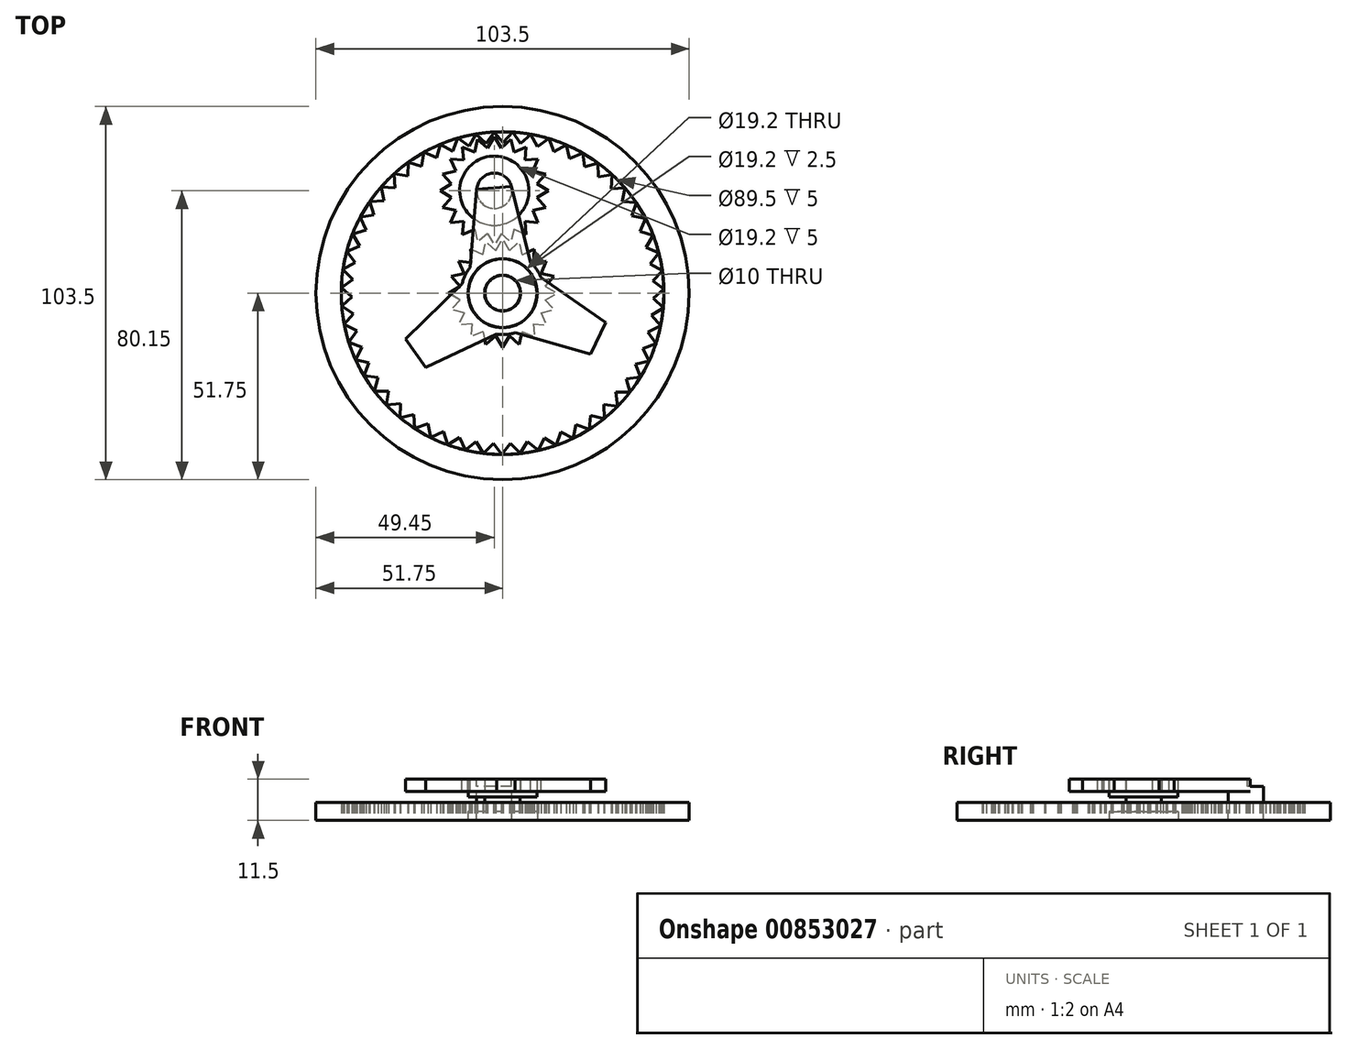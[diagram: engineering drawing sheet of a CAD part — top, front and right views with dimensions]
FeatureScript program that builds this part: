
annotation { "Feature Type Name" : "Feature", "Feature Type Description" : "" }
export const myFeature = defineFeature(function(context is Context, id is Id, definition is map)
    precondition{}
    {
        {
            var Q0;
            Q0=qCreatedBy(makeId("Top.planeOp"),FACE);
            var sketch = newSketch(context, id + "F0", { "sketchPlane" : qUnion([Q0])});
            skCircle(sketch, "E0", {"center": v(0, 0) * mm, "radius": 15 * mm});
            skLineSegment(sketch, "E1", {"start": v(0, 0) * mm, "end": v(0, 15) * mm, "construction": true});
            skCircle(sketch, "E2", {"center": v(0, 0) * mm, "radius": 12 * mm});
            skLineSegment(sketch, "E3", {"start": v(0, 0) * mm, "end": v(1.88, 11.85) * mm, "construction": true});
            skLineSegment(sketch, "E4", {"start": v(1.88, 11.85) * mm, "end": v(0, 15) * mm});
            skLineSegment(sketch, "E5.MirrorCS", {"start": v(-1.88, 11.85) * mm, "end": v(0, 15) * mm});
            skLineSegment(sketch, "E6.1.0", {"start": v(5.45, 10.7) * mm, "end": v(4.64, 14.27) * mm});
            skLineSegment(sketch, "E6.1.1", {"start": v(1.88, 11.85) * mm, "end": v(4.64, 14.27) * mm});
            skLineSegment(sketch, "E6.2.0", {"start": v(8.49, 8.49) * mm, "end": v(8.82, 12.14) * mm});
            skLineSegment(sketch, "E6.2.1", {"start": v(5.45, 10.7) * mm, "end": v(8.82, 12.14) * mm});
            skLineSegment(sketch, "E6.3.0", {"start": v(10.7, 5.45) * mm, "end": v(12.14, 8.82) * mm});
            skLineSegment(sketch, "E6.3.1", {"start": v(8.49, 8.49) * mm, "end": v(12.14, 8.82) * mm});
            skLineSegment(sketch, "E6.4.0", {"start": v(11.85, 1.88) * mm, "end": v(14.27, 4.64) * mm});
            skLineSegment(sketch, "E6.4.1", {"start": v(10.7, 5.45) * mm, "end": v(14.27, 4.64) * mm});
            skLineSegment(sketch, "E6.5.0", {"start": v(11.85, -1.88) * mm, "end": v(15, 0) * mm});
            skLineSegment(sketch, "E6.5.1", {"start": v(11.85, 1.88) * mm, "end": v(15, 0) * mm});
            skLineSegment(sketch, "E6.6.0", {"start": v(10.7, -5.45) * mm, "end": v(14.27, -4.64) * mm});
            skLineSegment(sketch, "E6.6.1", {"start": v(11.85, -1.88) * mm, "end": v(14.27, -4.64) * mm});
            skLineSegment(sketch, "E6.7.0", {"start": v(8.49, -8.49) * mm, "end": v(12.14, -8.82) * mm});
            skLineSegment(sketch, "E6.7.1", {"start": v(10.7, -5.45) * mm, "end": v(12.14, -8.82) * mm});
            skLineSegment(sketch, "E6.8.0", {"start": v(5.45, -10.7) * mm, "end": v(8.82, -12.14) * mm});
            skLineSegment(sketch, "E6.8.1", {"start": v(8.49, -8.49) * mm, "end": v(8.82, -12.14) * mm});
            skLineSegment(sketch, "E6.9.0", {"start": v(1.88, -11.85) * mm, "end": v(4.64, -14.27) * mm});
            skLineSegment(sketch, "E6.9.1", {"start": v(5.45, -10.7) * mm, "end": v(4.64, -14.27) * mm});
            skLineSegment(sketch, "E6.anchor2", {"start": v(0, 0) * mm, "end": v(1.88, -11.85) * mm, "construction": true});
            skLineSegment(sketch, "E7.MirrorCS", {"start": v(-1.88, 11.85) * mm, "end": v(-4.64, 14.27) * mm});
            skLineSegment(sketch, "E8.MirrorCS", {"start": v(-5.45, 10.7) * mm, "end": v(-4.64, 14.27) * mm});
            skLineSegment(sketch, "E9.MirrorCS", {"start": v(-5.45, 10.7) * mm, "end": v(-8.82, 12.14) * mm});
            skLineSegment(sketch, "E10.MirrorCS", {"start": v(-8.49, 8.49) * mm, "end": v(-8.82, 12.14) * mm});
            skLineSegment(sketch, "E11.MirrorCS", {"start": v(-8.49, 8.49) * mm, "end": v(-12.14, 8.82) * mm});
            skLineSegment(sketch, "E12.MirrorCS", {"start": v(-10.7, 5.45) * mm, "end": v(-12.14, 8.82) * mm});
            skLineSegment(sketch, "E13.MirrorCS", {"start": v(-10.7, 5.45) * mm, "end": v(-14.27, 4.64) * mm});
            skLineSegment(sketch, "E14.MirrorCS", {"start": v(-11.85, 1.88) * mm, "end": v(-14.27, 4.64) * mm});
            skLineSegment(sketch, "E15.MirrorCS", {"start": v(-11.85, 1.88) * mm, "end": v(-15, 0) * mm});
            skLineSegment(sketch, "E16.MirrorCS", {"start": v(-11.85, -1.88) * mm, "end": v(-15, 0) * mm});
            skLineSegment(sketch, "E17.MirrorCS", {"start": v(-11.85, -1.88) * mm, "end": v(-14.27, -4.64) * mm});
            skLineSegment(sketch, "E18.MirrorCS", {"start": v(-10.7, -5.45) * mm, "end": v(-14.27, -4.64) * mm});
            skLineSegment(sketch, "E19.MirrorCS", {"start": v(-10.7, -5.45) * mm, "end": v(-12.14, -8.82) * mm});
            skLineSegment(sketch, "E20.MirrorCS", {"start": v(-8.49, -8.49) * mm, "end": v(-12.14, -8.82) * mm});
            skLineSegment(sketch, "E21.MirrorCS", {"start": v(-8.49, -8.49) * mm, "end": v(-8.82, -12.14) * mm});
            skLineSegment(sketch, "E22.MirrorCS", {"start": v(-5.45, -10.7) * mm, "end": v(-8.82, -12.14) * mm});
            skLineSegment(sketch, "E23.MirrorCS", {"start": v(-5.45, -10.7) * mm, "end": v(-4.64, -14.27) * mm});
            skLineSegment(sketch, "E24.MirrorCS", {"start": v(-1.88, -11.85) * mm, "end": v(-4.64, -14.27) * mm});
            skLineSegment(sketch, "E25.MirrorCS", {"start": v(-1.88, -11.85) * mm, "end": v(0, -15) * mm});
            skLineSegment(sketch, "E26.MirrorCS", {"start": v(1.88, -11.85) * mm, "end": v(0, -15) * mm});
            skCircle(sketch, "E27", {"center": v(0, 0) * mm, "radius": 9.6 * mm});
            skSolve(sketch);
        }
        {
            var Q0;
            {var subQ0=sQuery(id+"F0.wireOp",EDGE,"E2");var subQ8=makeQuery(id+"F0.imprint","INTERSECT",VERTEX,{"derivedFrom":[subQ0,sQuery(id+"F0.wireOp",EDGE,"E6.3.0"),sQuery(id+"F0.wireOp",EDGE,"E6.4.1")]});Q0=makeQuery(id+"F0.imprint","IMPRINT",FACE,{"disambiguationData":[TD([[makeQuery(id+"F0.imprint","IMPRINT",EDGE,{"disambiguationData":[TD([[subQ8,1.0]])],"derivedFrom":subQ0}),1.0]])]});}
            var Q1;
            {var subQ0=sQuery(id+"F0.wireOp",EDGE,"E7.MirrorCS");Q1=makeQuery(id+"F0.imprint","IMPRINT",FACE,{"disambiguationData":[TD([[makeQuery(id+"F0.imprint","IMPRINT",EDGE,{"derivedFrom":subQ0}),1.0]])]});}
            var Q2;
            {var subQ0=sQuery(id+"F0.wireOp",EDGE,"E4");Q2=makeQuery(id+"F0.imprint","IMPRINT",FACE,{"disambiguationData":[TD([[makeQuery(id+"F0.imprint","IMPRINT",EDGE,{"derivedFrom":subQ0}),1.0]])]});}
            var Q3;
            {var subQ2=sQuery(id+"F0.wireOp",EDGE,"E6.1.0");Q3=makeQuery(id+"F0.imprint","IMPRINT",FACE,{"disambiguationData":[TD([[makeQuery(id+"F0.imprint","IMPRINT",EDGE,{"derivedFrom":subQ2}),1.0]])]});}
            var Q4;
            {var subQ2=sQuery(id+"F0.wireOp",EDGE,"E6.2.0");Q4=makeQuery(id+"F0.imprint","IMPRINT",FACE,{"disambiguationData":[TD([[makeQuery(id+"F0.imprint","IMPRINT",EDGE,{"derivedFrom":subQ2}),1.0]])]});}
            var Q5;
            {var subQ2=sQuery(id+"F0.wireOp",EDGE,"E6.3.0");Q5=makeQuery(id+"F0.imprint","IMPRINT",FACE,{"disambiguationData":[TD([[makeQuery(id+"F0.imprint","IMPRINT",EDGE,{"derivedFrom":subQ2}),1.0]])]});}
            var Q6;
            {var subQ2=sQuery(id+"F0.wireOp",EDGE,"E6.4.0");Q6=makeQuery(id+"F0.imprint","IMPRINT",FACE,{"disambiguationData":[TD([[makeQuery(id+"F0.imprint","IMPRINT",EDGE,{"derivedFrom":subQ2}),1.0]])]});}
            var Q7;
            {var subQ2=sQuery(id+"F0.wireOp",EDGE,"E6.5.0");Q7=makeQuery(id+"F0.imprint","IMPRINT",FACE,{"disambiguationData":[TD([[makeQuery(id+"F0.imprint","IMPRINT",EDGE,{"derivedFrom":subQ2}),1.0]])]});}
            var Q8;
            {var subQ2=sQuery(id+"F0.wireOp",EDGE,"E6.6.0");Q8=makeQuery(id+"F0.imprint","IMPRINT",FACE,{"disambiguationData":[TD([[makeQuery(id+"F0.imprint","IMPRINT",EDGE,{"derivedFrom":subQ2}),1.0]])]});}
            var Q9;
            {var subQ2=sQuery(id+"F0.wireOp",EDGE,"E6.7.0");Q9=makeQuery(id+"F0.imprint","IMPRINT",FACE,{"disambiguationData":[TD([[makeQuery(id+"F0.imprint","IMPRINT",EDGE,{"derivedFrom":subQ2}),1.0]])]});}
            var Q10;
            {var subQ2=sQuery(id+"F0.wireOp",EDGE,"E6.8.0");Q10=makeQuery(id+"F0.imprint","IMPRINT",FACE,{"disambiguationData":[TD([[makeQuery(id+"F0.imprint","IMPRINT",EDGE,{"derivedFrom":subQ2}),1.0]])]});}
            var Q11;
            {var subQ2=sQuery(id+"F0.wireOp",EDGE,"E6.9.0");Q11=makeQuery(id+"F0.imprint","IMPRINT",FACE,{"disambiguationData":[TD([[makeQuery(id+"F0.imprint","IMPRINT",EDGE,{"derivedFrom":subQ2}),1.0]])]});}
            var Q12;
            {var subQ2=sQuery(id+"F0.wireOp",EDGE,"E25.MirrorCS");Q12=makeQuery(id+"F0.imprint","IMPRINT",FACE,{"disambiguationData":[TD([[makeQuery(id+"F0.imprint","IMPRINT",EDGE,{"derivedFrom":subQ2}),1.0]])]});}
            var Q13;
            {var subQ0=sQuery(id+"F0.wireOp",EDGE,"E23.MirrorCS");Q13=makeQuery(id+"F0.imprint","IMPRINT",FACE,{"disambiguationData":[TD([[makeQuery(id+"F0.imprint","IMPRINT",EDGE,{"derivedFrom":subQ0}),1.0]])]});}
            var Q14;
            {var subQ0=sQuery(id+"F0.wireOp",EDGE,"E21.MirrorCS");Q14=makeQuery(id+"F0.imprint","IMPRINT",FACE,{"disambiguationData":[TD([[makeQuery(id+"F0.imprint","IMPRINT",EDGE,{"derivedFrom":subQ0}),1.0]])]});}
            var Q15;
            {var subQ0=sQuery(id+"F0.wireOp",EDGE,"E19.MirrorCS");Q15=makeQuery(id+"F0.imprint","IMPRINT",FACE,{"disambiguationData":[TD([[makeQuery(id+"F0.imprint","IMPRINT",EDGE,{"derivedFrom":subQ0}),1.0]])]});}
            var Q16;
            {var subQ0=sQuery(id+"F0.wireOp",EDGE,"E17.MirrorCS");Q16=makeQuery(id+"F0.imprint","IMPRINT",FACE,{"disambiguationData":[TD([[makeQuery(id+"F0.imprint","IMPRINT",EDGE,{"derivedFrom":subQ0}),1.0]])]});}
            var Q17;
            {var subQ0=sQuery(id+"F0.wireOp",EDGE,"E15.MirrorCS");Q17=makeQuery(id+"F0.imprint","IMPRINT",FACE,{"disambiguationData":[TD([[makeQuery(id+"F0.imprint","IMPRINT",EDGE,{"derivedFrom":subQ0}),1.0]])]});}
            var Q18;
            {var subQ0=sQuery(id+"F0.wireOp",EDGE,"E13.MirrorCS");Q18=makeQuery(id+"F0.imprint","IMPRINT",FACE,{"disambiguationData":[TD([[makeQuery(id+"F0.imprint","IMPRINT",EDGE,{"derivedFrom":subQ0}),1.0]])]});}
            var Q19;
            {var subQ0=sQuery(id+"F0.wireOp",EDGE,"E11.MirrorCS");Q19=makeQuery(id+"F0.imprint","IMPRINT",FACE,{"disambiguationData":[TD([[makeQuery(id+"F0.imprint","IMPRINT",EDGE,{"derivedFrom":subQ0}),1.0]])]});}
            var Q20;
            {var subQ0=sQuery(id+"F0.wireOp",EDGE,"E9.MirrorCS");Q20=makeQuery(id+"F0.imprint","IMPRINT",FACE,{"disambiguationData":[TD([[makeQuery(id+"F0.imprint","IMPRINT",EDGE,{"derivedFrom":subQ0}),1.0]])]});}
            extrude(context, id + "F1", {"entities" : qUnion([Q0, Q1, Q2, Q3, Q4, Q5, Q6, Q7, Q8, Q9, Q10, Q11, Q12, Q13, Q14, Q15, Q16, Q17, Q18, Q19, Q20]), "endBound" : BoundingType.SYMMETRIC, "depth" : 5 * mm, "offsetDistance" : 25 * mm});
        }
        {
            var Q0;
            Q0=qCreatedBy(makeId("Front.planeOp"),FACE);
            var sketch = newSketch(context, id + "F2", { "sketchPlane" : qUnion([Q0])});
            skLineSegment(sketch, "E28", {"start": v(0, 0) * mm, "end": v(0, 25.45) * mm, "construction": true});
            skSolve(sketch);
        }
        {
            var Q0;
            Q0=qCreatedBy(makeId("Top.planeOp"),FACE);
            var sketch = newSketch(context, id + "F3", { "sketchPlane" : qUnion([Q0])});
            skCircle(sketch, "E29", {"center": v(0, 0) * mm, "radius": 41.75 * mm});
            skCircle(sketch, "E30.0", {"center": v(0, 0) * mm, "radius": 51.75 * mm});
            skCircle(sketch, "E31.0", {"center": v(0, 0) * mm, "radius": 44.75 * mm});
            skLineSegment(sketch, "E32", {"start": v(0, 0) * mm, "end": v(44.55, -4.2) * mm, "construction": true});
            skLineSegment(sketch, "E33", {"start": v(0, 0) * mm, "end": v(44.24, -6.74) * mm, "construction": true});
            skLineSegment(sketch, "E34", {"start": v(0, 0) * mm, "end": v(44.75, 0) * mm, "construction": true});
            skLineSegment(sketch, "E35", {"start": v(44.24, -6.74) * mm, "end": v(41.57, -3.92) * mm});
            skLineSegment(sketch, "E36.MirrorCS", {"start": v(44.72, -1.64) * mm, "end": v(41.57, -3.92) * mm});
            skLineSegment(sketch, "E37.1.0", {"start": v(43.16, -11.83) * mm, "end": v(40.83, -8.72) * mm});
            skLineSegment(sketch, "E37.1.1", {"start": v(44.23, -6.82) * mm, "end": v(40.83, -8.72) * mm});
            skLineSegment(sketch, "E37.2.0", {"start": v(41.5, -16.76) * mm, "end": v(39.54, -13.4) * mm});
            skLineSegment(sketch, "E37.2.1", {"start": v(43.14, -11.9) * mm, "end": v(39.54, -13.4) * mm});
            skLineSegment(sketch, "E37.3.0", {"start": v(39.26, -21.47) * mm, "end": v(37.72, -17.9) * mm});
            skLineSegment(sketch, "E37.3.1", {"start": v(41.46, -16.83) * mm, "end": v(37.72, -17.9) * mm});
            skLineSegment(sketch, "E37.4.0", {"start": v(36.5, -25.88) * mm, "end": v(35.39, -22.15) * mm});
            skLineSegment(sketch, "E37.4.1", {"start": v(39.23, -21.53) * mm, "end": v(35.39, -22.15) * mm});
            skLineSegment(sketch, "E37.5.0", {"start": v(33.25, -29.94) * mm, "end": v(32.58, -26.11) * mm});
            skLineSegment(sketch, "E37.5.1", {"start": v(36.46, -25.94) * mm, "end": v(32.58, -26.11) * mm});
            skLineSegment(sketch, "E37.6.0", {"start": v(29.55, -33.6) * mm, "end": v(29.32, -29.72) * mm});
            skLineSegment(sketch, "E37.6.1", {"start": v(33.2, -30) * mm, "end": v(29.32, -29.72) * mm});
            skLineSegment(sketch, "E37.7.0", {"start": v(25.45, -36.8) * mm, "end": v(25.68, -32.92) * mm});
            skLineSegment(sketch, "E37.7.1", {"start": v(29.5, -33.65) * mm, "end": v(25.68, -32.92) * mm});
            skLineSegment(sketch, "E37.8.0", {"start": v(21, -39.51) * mm, "end": v(21.68, -35.68) * mm});
            skLineSegment(sketch, "E37.8.1", {"start": v(25.4, -36.85) * mm, "end": v(21.68, -35.68) * mm});
            skLineSegment(sketch, "E37.9.0", {"start": v(16.28, -41.68) * mm, "end": v(17.4, -37.96) * mm});
            skLineSegment(sketch, "E37.9.1", {"start": v(20.94, -39.55) * mm, "end": v(17.4, -37.96) * mm});
            skLineSegment(sketch, "E37.anchor2", {"start": v(0, 0) * mm, "end": v(16.28, -41.68) * mm, "construction": true});
            skLineSegment(sketch, "E38.1.0", {"start": v(16.33, -41.66) * mm, "end": v(12.98, -39.68) * mm});
            skLineSegment(sketch, "E38.1.1", {"start": v(11.46, -43.26) * mm, "end": v(12.98, -39.68) * mm});
            skLineSegment(sketch, "E38.1.2", {"start": v(11.38, -43.28) * mm, "end": v(8.29, -40.92) * mm});
            skLineSegment(sketch, "E38.1.3", {"start": v(6.36, -44.3) * mm, "end": v(8.29, -40.92) * mm});
            skLineSegment(sketch, "E38.1.4", {"start": v(6.28, -44.3) * mm, "end": v(3.48, -41.6) * mm});
            skLineSegment(sketch, "E38.1.5", {"start": v(1.17, -44.73) * mm, "end": v(3.48, -41.6) * mm});
            skLineSegment(sketch, "E38.1.6", {"start": v(1.1, -44.74) * mm, "end": v(-1.37, -41.73) * mm});
            skLineSegment(sketch, "E38.1.7", {"start": v(-4.03, -44.57) * mm, "end": v(-1.37, -41.73) * mm});
            skLineSegment(sketch, "E38.1.8", {"start": v(-4.1, -44.56) * mm, "end": v(-6.2, -41.29) * mm});
            skLineSegment(sketch, "E38.1.9", {"start": v(-9.18, -43.8) * mm, "end": v(-6.2, -41.29) * mm});
            skLineSegment(sketch, "E38.1.10", {"start": v(-9.25, -43.78) * mm, "end": v(-10.96, -40.29) * mm});
            skLineSegment(sketch, "E38.1.11", {"start": v(-14.2, -42.44) * mm, "end": v(-10.96, -40.29) * mm});
            skLineSegment(sketch, "E38.1.12", {"start": v(-14.27, -42.41) * mm, "end": v(-15.56, -38.74) * mm});
            skLineSegment(sketch, "E38.1.13", {"start": v(-19.03, -40.5) * mm, "end": v(-15.56, -38.74) * mm});
            skLineSegment(sketch, "E38.1.14", {"start": v(-19.1, -40.47) * mm, "end": v(-19.95, -36.67) * mm});
            skLineSegment(sketch, "E38.1.15", {"start": v(-23.6, -38.02) * mm, "end": v(-19.95, -36.67) * mm});
            skLineSegment(sketch, "E38.1.16", {"start": v(-23.67, -37.98) * mm, "end": v(-24.08, -34.1) * mm});
            skLineSegment(sketch, "E38.1.17", {"start": v(-27.86, -35.02) * mm, "end": v(-24.08, -34.1) * mm});
            skLineSegment(sketch, "E38.1.18", {"start": v(-27.92, -34.97) * mm, "end": v(-27.87, -31.08) * mm});
            skLineSegment(sketch, "E38.1.19", {"start": v(-31.74, -31.55) * mm, "end": v(-27.87, -31.08) * mm});
            skLineSegment(sketch, "E38.2.0", {"start": v(-31.7, -31.59) * mm, "end": v(-31.21, -27.73) * mm});
            skLineSegment(sketch, "E38.2.1", {"start": v(-35.1, -27.75) * mm, "end": v(-31.21, -27.73) * mm});
            skLineSegment(sketch, "E38.2.2", {"start": v(-35.15, -27.7) * mm, "end": v(-34.22, -23.92) * mm});
            skLineSegment(sketch, "E38.2.3", {"start": v(-38.09, -23.5) * mm, "end": v(-34.22, -23.92) * mm});
            skLineSegment(sketch, "E38.2.4", {"start": v(-38.13, -23.43) * mm, "end": v(-36.77, -19.78) * mm});
            skLineSegment(sketch, "E38.2.5", {"start": v(-40.56, -18.91) * mm, "end": v(-36.77, -19.78) * mm});
            skLineSegment(sketch, "E38.2.6", {"start": v(-40.59, -18.84) * mm, "end": v(-38.81, -15.38) * mm});
            skLineSegment(sketch, "E38.2.7", {"start": v(-42.48, -14.07) * mm, "end": v(-38.81, -15.38) * mm});
            skLineSegment(sketch, "E38.2.8", {"start": v(-42.5, -14) * mm, "end": v(-40.34, -10.77) * mm});
            skLineSegment(sketch, "E38.2.9", {"start": v(-43.83, -9.05) * mm, "end": v(-40.34, -10.77) * mm});
            skLineSegment(sketch, "E38.2.10", {"start": v(-43.84, -8.97) * mm, "end": v(-41.31, -6.01) * mm});
            skLineSegment(sketch, "E38.2.11", {"start": v(-44.58, -3.9) * mm, "end": v(-41.31, -6.01) * mm});
            skLineSegment(sketch, "E38.2.12", {"start": v(-44.59, -3.82) * mm, "end": v(-41.73, -1.18) * mm});
            skLineSegment(sketch, "E38.2.13", {"start": v(-44.73, 1.3) * mm, "end": v(-41.73, -1.18) * mm});
            skLineSegment(sketch, "E38.2.14", {"start": v(-44.73, 1.38) * mm, "end": v(-41.59, 3.67) * mm});
            skLineSegment(sketch, "E38.2.15", {"start": v(-44.28, 6.49) * mm, "end": v(-41.59, 3.67) * mm});
            skLineSegment(sketch, "E38.2.16", {"start": v(-44.27, 6.56) * mm, "end": v(-40.88, 8.48) * mm});
            skLineSegment(sketch, "E38.2.17", {"start": v(-43.22, 11.58) * mm, "end": v(-40.88, 8.48) * mm});
            skLineSegment(sketch, "E38.2.18", {"start": v(-43.2, 11.66) * mm, "end": v(-39.62, 13.17) * mm});
            skLineSegment(sketch, "E38.2.19", {"start": v(-41.59, 16.52) * mm, "end": v(-39.62, 13.17) * mm});
            skLineSegment(sketch, "E38.anchor1", {"start": v(0, 0) * mm, "end": v(41.57, -3.92) * mm, "construction": true});
            skLineSegment(sketch, "E38.anchor2", {"start": v(0, 0) * mm, "end": v(-31.21, -27.73) * mm, "construction": true});
            skLineSegment(sketch, "E39.MirrorCS", {"start": v(44.72, -1.56) * mm, "end": v(41.74, 0.94) * mm});
            skLineSegment(sketch, "E40.MirrorCS", {"start": v(44.6, 3.56) * mm, "end": v(41.74, 0.94) * mm});
            skLineSegment(sketch, "E41.MirrorCS", {"start": v(44.6, 3.64) * mm, "end": v(41.35, 5.77) * mm});
            skLineSegment(sketch, "E42.MirrorCS", {"start": v(43.9, 8.72) * mm, "end": v(41.35, 5.77) * mm});
            skLineSegment(sketch, "E43.MirrorCS", {"start": v(43.88, 8.8) * mm, "end": v(40.4, 10.54) * mm});
            skLineSegment(sketch, "E44.MirrorCS", {"start": v(42.58, 13.76) * mm, "end": v(40.4, 10.54) * mm});
            skLineSegment(sketch, "E45.MirrorCS", {"start": v(42.56, 13.83) * mm, "end": v(38.9, 15.15) * mm});
            skLineSegment(sketch, "E46.MirrorCS", {"start": v(40.7, 18.6) * mm, "end": v(38.9, 15.15) * mm});
            skLineSegment(sketch, "E47.MirrorCS", {"start": v(40.67, 18.67) * mm, "end": v(36.88, 19.57) * mm});
            skLineSegment(sketch, "E48.MirrorCS", {"start": v(38.26, 23.2) * mm, "end": v(36.88, 19.57) * mm});
            skLineSegment(sketch, "E49.MirrorCS", {"start": v(38.22, 23.27) * mm, "end": v(34.36, 23.72) * mm});
            skLineSegment(sketch, "E50.MirrorCS", {"start": v(35.31, 27.5) * mm, "end": v(34.36, 23.72) * mm});
            skLineSegment(sketch, "E51.MirrorCS", {"start": v(35.26, 27.55) * mm, "end": v(31.37, 27.55) * mm});
            skLineSegment(sketch, "E52.MirrorCS", {"start": v(31.88, 31.4) * mm, "end": v(31.37, 27.55) * mm});
            skLineSegment(sketch, "E53.MirrorCS", {"start": v(31.83, 31.46) * mm, "end": v(27.96, 31) * mm});
            skLineSegment(sketch, "E54.MirrorCS", {"start": v(28.02, 34.9) * mm, "end": v(27.96, 31) * mm});
            skLineSegment(sketch, "E55.MirrorCS", {"start": v(27.96, 34.94) * mm, "end": v(24.17, 34.04) * mm});
            skLineSegment(sketch, "E56.MirrorCS", {"start": v(23.78, 37.9) * mm, "end": v(24.17, 34.04) * mm});
            skLineSegment(sketch, "E57.MirrorCS", {"start": v(23.83, 37.88) * mm, "end": v(20.17, 36.56) * mm});
            skLineSegment(sketch, "E58.MirrorCS", {"start": v(19.33, 40.36) * mm, "end": v(20.17, 36.56) * mm});
            skLineSegment(sketch, "E59.MirrorCS", {"start": v(19.27, 40.4) * mm, "end": v(15.79, 38.65) * mm});
            skLineSegment(sketch, "E60.MirrorCS", {"start": v(14.52, 42.33) * mm, "end": v(15.79, 38.65) * mm});
            skLineSegment(sketch, "E61.MirrorCS", {"start": v(14.45, 42.35) * mm, "end": v(11.2, 40.22) * mm});
            skLineSegment(sketch, "E62.MirrorCS", {"start": v(9.5, 43.73) * mm, "end": v(11.2, 40.22) * mm});
            skLineSegment(sketch, "E63.MirrorCS", {"start": v(4.37, 44.54) * mm, "end": v(6.45, 41.25) * mm});
            skLineSegment(sketch, "E64.MirrorCS", {"start": v(9.43, 43.74) * mm, "end": v(6.45, 41.25) * mm});
            skLineSegment(sketch, "E65.MirrorCS", {"start": v(4.3, 44.54) * mm, "end": v(1.61, 41.72) * mm});
            skLineSegment(sketch, "E66.MirrorCS", {"start": v(-0.83, 44.74) * mm, "end": v(1.61, 41.72) * mm});
            skLineSegment(sketch, "E67.MirrorCS", {"start": v(-0.9, 44.74) * mm, "end": v(-3.24, 41.62) * mm});
            skLineSegment(sketch, "E68.MirrorCS", {"start": v(-6.02, 44.34) * mm, "end": v(-3.24, 41.62) * mm});
            skLineSegment(sketch, "E69.MirrorCS", {"start": v(-6.1, 44.33) * mm, "end": v(-8.05, 40.97) * mm});
            skLineSegment(sketch, "E70.MirrorCS", {"start": v(-11.13, 43.34) * mm, "end": v(-8.05, 40.97) * mm});
            skLineSegment(sketch, "E71.MirrorCS", {"start": v(-11.2, 43.32) * mm, "end": v(-12.75, 39.76) * mm});
            skLineSegment(sketch, "E72.MirrorCS", {"start": v(-16.09, 41.76) * mm, "end": v(-12.75, 39.76) * mm});
            skLineSegment(sketch, "E73.MirrorCS", {"start": v(-16.16, 41.73) * mm, "end": v(-17.28, 38) * mm});
            skLineSegment(sketch, "E74.MirrorCS", {"start": v(-20.83, 39.6) * mm, "end": v(-17.28, 38) * mm});
            skLineSegment(sketch, "E75.MirrorCS", {"start": v(-20.9, 39.57) * mm, "end": v(-21.58, 35.74) * mm});
            skLineSegment(sketch, "E76.MirrorCS", {"start": v(-25.28, 36.92) * mm, "end": v(-21.58, 35.74) * mm});
            skLineSegment(sketch, "E77.MirrorCS", {"start": v(-25.24, 36.95) * mm, "end": v(-25.48, 33.07) * mm});
            skLineSegment(sketch, "E78.MirrorCS", {"start": v(-29.3, 33.82) * mm, "end": v(-25.48, 33.07) * mm});
            skLineSegment(sketch, "E79.MirrorCS", {"start": v(-29.36, 33.77) * mm, "end": v(-29.15, 29.89) * mm});
            skLineSegment(sketch, "E80.MirrorCS", {"start": v(-33.03, 30.2) * mm, "end": v(-29.15, 29.89) * mm});
            skLineSegment(sketch, "E81.MirrorCS", {"start": v(-33.08, 30.14) * mm, "end": v(-32.42, 26.3) * mm});
            skLineSegment(sketch, "E82.MirrorCS", {"start": v(-36.31, 26.15) * mm, "end": v(-32.42, 26.3) * mm});
            skLineSegment(sketch, "E83.MirrorCS", {"start": v(-36.36, 26.1) * mm, "end": v(-35.26, 22.36) * mm});
            skLineSegment(sketch, "E84.MirrorCS", {"start": v(-39.1, 21.76) * mm, "end": v(-35.26, 22.36) * mm});
            skLineSegment(sketch, "E85.MirrorCS", {"start": v(-39.14, 21.7) * mm, "end": v(-37.61, 18.12) * mm});
            skLineSegment(sketch, "E86.MirrorCS", {"start": v(-41.36, 17.08) * mm, "end": v(-37.61, 18.12) * mm});
            skSolve(sketch);
        }
        {
            var Q0;
            Q0=makeQuery(id+"F3.imprint","IMPRINT",FACE,{"disambiguationData":[TD([[makeQuery(id+"F3.imprint","IMPRINT",EDGE,{"derivedFrom":sQuery(id+"F3.wireOp",EDGE,"E30.0")}),1.0]])]});
            extrude(context, id + "F4", {"entities" : qUnion([Q0]), "endBound" : BoundingType.SYMMETRIC, "depth" : 5 * mm, "offsetDistance" : 25 * mm});
        }
        {
            var Q0;
            {var subQ0=sQuery(id+"F3.wireOp",EDGE,"E38.2.16");Q0=makeQuery(id+"F3.imprint","IMPRINT",FACE,{"disambiguationData":[TD([[makeQuery(id+"F3.imprint","IMPRINT",EDGE,{"derivedFrom":subQ0}),1.0]])]});}
            extrude(context, id + "F5", {"entities" : qUnion([Q0]), "endBound" : BoundingType.SYMMETRIC, "depth" : 5 * mm, "offsetDistance" : 25 * mm});
        }
        {
            var Q0;
            Q0=makeQuery(id+"F5.opExtrude","SWEPT_BODY",BODY,{"disambiguationData":[OSD([sQuery(id+"F3.wireOp",EDGE,"E31.0"),sQuery(id+"F3.wireOp",EDGE,"E38.2.16"),sQuery(id+"F3.wireOp",EDGE,"E38.2.17")])]});
            var Q1;
            Q1=sQuery(id+"F2.wireOp",EDGE,"E28");
            circularPattern(context, id + "F6", {"entities" : qUnion([Q0]), "axis" : qUnion([Q1]), "angle" : 360 * degree, "instanceCount" : 55, "equalSpace" : true});
        }
        {
            var Q0;
            Q0=makeQuery(id+"F1.opExtrude","SWEPT_BODY",BODY,{"disambiguationData":[OSD([sQuery(id+"F0.wireOp",EDGE,"E4"),sQuery(id+"F0.wireOp",EDGE,"E5.MirrorCS"),sQuery(id+"F0.wireOp",EDGE,"E6.1.0"),sQuery(id+"F0.wireOp",EDGE,"E6.1.1"),sQuery(id+"F0.wireOp",EDGE,"E6.2.0"),sQuery(id+"F0.wireOp",EDGE,"E6.2.1"),sQuery(id+"F0.wireOp",EDGE,"E6.3.0"),sQuery(id+"F0.wireOp",EDGE,"E6.3.1"),sQuery(id+"F0.wireOp",EDGE,"E6.4.0"),sQuery(id+"F0.wireOp",EDGE,"E6.4.1"),sQuery(id+"F0.wireOp",EDGE,"E6.5.0"),sQuery(id+"F0.wireOp",EDGE,"E6.5.1"),sQuery(id+"F0.wireOp",EDGE,"E6.6.0"),sQuery(id+"F0.wireOp",EDGE,"E6.6.1"),sQuery(id+"F0.wireOp",EDGE,"E6.7.0"),sQuery(id+"F0.wireOp",EDGE,"E6.7.1"),sQuery(id+"F0.wireOp",EDGE,"E6.8.0"),sQuery(id+"F0.wireOp",EDGE,"E6.8.1"),sQuery(id+"F0.wireOp",EDGE,"E6.9.0"),sQuery(id+"F0.wireOp",EDGE,"E6.9.1"),sQuery(id+"F0.wireOp",EDGE,"E7.MirrorCS"),sQuery(id+"F0.wireOp",EDGE,"E8.MirrorCS"),sQuery(id+"F0.wireOp",EDGE,"E9.MirrorCS"),sQuery(id+"F0.wireOp",EDGE,"E10.MirrorCS"),sQuery(id+"F0.wireOp",EDGE,"E11.MirrorCS"),sQuery(id+"F0.wireOp",EDGE,"E12.MirrorCS"),sQuery(id+"F0.wireOp",EDGE,"E13.MirrorCS"),sQuery(id+"F0.wireOp",EDGE,"E14.MirrorCS"),sQuery(id+"F0.wireOp",EDGE,"E15.MirrorCS"),sQuery(id+"F0.wireOp",EDGE,"E16.MirrorCS"),sQuery(id+"F0.wireOp",EDGE,"E17.MirrorCS"),sQuery(id+"F0.wireOp",EDGE,"E18.MirrorCS"),sQuery(id+"F0.wireOp",EDGE,"E19.MirrorCS"),sQuery(id+"F0.wireOp",EDGE,"E20.MirrorCS"),sQuery(id+"F0.wireOp",EDGE,"E21.MirrorCS"),sQuery(id+"F0.wireOp",EDGE,"E22.MirrorCS"),sQuery(id+"F0.wireOp",EDGE,"E23.MirrorCS"),sQuery(id+"F0.wireOp",EDGE,"E24.MirrorCS"),sQuery(id+"F0.wireOp",EDGE,"E25.MirrorCS"),sQuery(id+"F0.wireOp",EDGE,"E26.MirrorCS"),sQuery(id+"F0.wireOp",EDGE,"E27")])]});
            transform(context, id + "F7", {"entities" : qUnion([Q0]), "transformType" : TransformType.TRANSLATION_3D, "dx" : -2.3 * mm, "dy" : 28.4 * mm, "dz" : 0 * mm, "makeCopy" : false});
        }
        {
            var Q0;
            Q0=makeQuery(id+"F0.imprint","IMPRINT",FACE,{"disambiguationData":[TD([[makeQuery(id+"F0.imprint","IMPRINT",EDGE,{"derivedFrom":sQuery(id+"F0.wireOp",EDGE,"E27")}),-1.0]])]});
            var Q1;
            {var subQ0=sQuery(id+"F0.wireOp",EDGE,"E9.MirrorCS");Q1=makeQuery(id+"F0.imprint","IMPRINT",FACE,{"disambiguationData":[TD([[makeQuery(id+"F0.imprint","IMPRINT",EDGE,{"derivedFrom":subQ0}),1.0]])]});}
            var Q2;
            {var subQ0=sQuery(id+"F0.wireOp",EDGE,"E7.MirrorCS");Q2=makeQuery(id+"F0.imprint","IMPRINT",FACE,{"disambiguationData":[TD([[makeQuery(id+"F0.imprint","IMPRINT",EDGE,{"derivedFrom":subQ0}),1.0]])]});}
            var Q3;
            {var subQ0=sQuery(id+"F0.wireOp",EDGE,"E4");Q3=makeQuery(id+"F0.imprint","IMPRINT",FACE,{"disambiguationData":[TD([[makeQuery(id+"F0.imprint","IMPRINT",EDGE,{"derivedFrom":subQ0}),1.0]])]});}
            var Q4;
            {var subQ2=sQuery(id+"F0.wireOp",EDGE,"E6.1.0");Q4=makeQuery(id+"F0.imprint","IMPRINT",FACE,{"disambiguationData":[TD([[makeQuery(id+"F0.imprint","IMPRINT",EDGE,{"derivedFrom":subQ2}),1.0]])]});}
            var Q5;
            {var subQ2=sQuery(id+"F0.wireOp",EDGE,"E6.2.0");Q5=makeQuery(id+"F0.imprint","IMPRINT",FACE,{"disambiguationData":[TD([[makeQuery(id+"F0.imprint","IMPRINT",EDGE,{"derivedFrom":subQ2}),1.0]])]});}
            var Q6;
            {var subQ2=sQuery(id+"F0.wireOp",EDGE,"E6.3.0");Q6=makeQuery(id+"F0.imprint","IMPRINT",FACE,{"disambiguationData":[TD([[makeQuery(id+"F0.imprint","IMPRINT",EDGE,{"derivedFrom":subQ2}),1.0]])]});}
            var Q7;
            {var subQ2=sQuery(id+"F0.wireOp",EDGE,"E6.4.0");Q7=makeQuery(id+"F0.imprint","IMPRINT",FACE,{"disambiguationData":[TD([[makeQuery(id+"F0.imprint","IMPRINT",EDGE,{"derivedFrom":subQ2}),1.0]])]});}
            var Q8;
            {var subQ2=sQuery(id+"F0.wireOp",EDGE,"E6.5.0");Q8=makeQuery(id+"F0.imprint","IMPRINT",FACE,{"disambiguationData":[TD([[makeQuery(id+"F0.imprint","IMPRINT",EDGE,{"derivedFrom":subQ2}),1.0]])]});}
            var Q9;
            {var subQ2=sQuery(id+"F0.wireOp",EDGE,"E6.6.0");Q9=makeQuery(id+"F0.imprint","IMPRINT",FACE,{"disambiguationData":[TD([[makeQuery(id+"F0.imprint","IMPRINT",EDGE,{"derivedFrom":subQ2}),1.0]])]});}
            var Q10;
            {var subQ2=sQuery(id+"F0.wireOp",EDGE,"E6.7.0");Q10=makeQuery(id+"F0.imprint","IMPRINT",FACE,{"disambiguationData":[TD([[makeQuery(id+"F0.imprint","IMPRINT",EDGE,{"derivedFrom":subQ2}),1.0]])]});}
            var Q11;
            {var subQ2=sQuery(id+"F0.wireOp",EDGE,"E6.8.0");Q11=makeQuery(id+"F0.imprint","IMPRINT",FACE,{"disambiguationData":[TD([[makeQuery(id+"F0.imprint","IMPRINT",EDGE,{"derivedFrom":subQ2}),1.0]])]});}
            var Q12;
            {var subQ2=sQuery(id+"F0.wireOp",EDGE,"E6.9.0");Q12=makeQuery(id+"F0.imprint","IMPRINT",FACE,{"disambiguationData":[TD([[makeQuery(id+"F0.imprint","IMPRINT",EDGE,{"derivedFrom":subQ2}),1.0]])]});}
            var Q13;
            {var subQ2=sQuery(id+"F0.wireOp",EDGE,"E25.MirrorCS");Q13=makeQuery(id+"F0.imprint","IMPRINT",FACE,{"disambiguationData":[TD([[makeQuery(id+"F0.imprint","IMPRINT",EDGE,{"derivedFrom":subQ2}),1.0]])]});}
            var Q14;
            {var subQ0=sQuery(id+"F0.wireOp",EDGE,"E23.MirrorCS");Q14=makeQuery(id+"F0.imprint","IMPRINT",FACE,{"disambiguationData":[TD([[makeQuery(id+"F0.imprint","IMPRINT",EDGE,{"derivedFrom":subQ0}),1.0]])]});}
            var Q15;
            {var subQ0=sQuery(id+"F0.wireOp",EDGE,"E21.MirrorCS");Q15=makeQuery(id+"F0.imprint","IMPRINT",FACE,{"disambiguationData":[TD([[makeQuery(id+"F0.imprint","IMPRINT",EDGE,{"derivedFrom":subQ0}),1.0]])]});}
            var Q16;
            {var subQ0=sQuery(id+"F0.wireOp",EDGE,"E19.MirrorCS");Q16=makeQuery(id+"F0.imprint","IMPRINT",FACE,{"disambiguationData":[TD([[makeQuery(id+"F0.imprint","IMPRINT",EDGE,{"derivedFrom":subQ0}),1.0]])]});}
            var Q17;
            {var subQ0=sQuery(id+"F0.wireOp",EDGE,"E17.MirrorCS");Q17=makeQuery(id+"F0.imprint","IMPRINT",FACE,{"disambiguationData":[TD([[makeQuery(id+"F0.imprint","IMPRINT",EDGE,{"derivedFrom":subQ0}),1.0]])]});}
            var Q18;
            {var subQ0=sQuery(id+"F0.wireOp",EDGE,"E15.MirrorCS");Q18=makeQuery(id+"F0.imprint","IMPRINT",FACE,{"disambiguationData":[TD([[makeQuery(id+"F0.imprint","IMPRINT",EDGE,{"derivedFrom":subQ0}),1.0]])]});}
            var Q19;
            {var subQ0=sQuery(id+"F0.wireOp",EDGE,"E13.MirrorCS");Q19=makeQuery(id+"F0.imprint","IMPRINT",FACE,{"disambiguationData":[TD([[makeQuery(id+"F0.imprint","IMPRINT",EDGE,{"derivedFrom":subQ0}),1.0]])]});}
            var Q20;
            {var subQ0=sQuery(id+"F0.wireOp",EDGE,"E11.MirrorCS");Q20=makeQuery(id+"F0.imprint","IMPRINT",FACE,{"disambiguationData":[TD([[makeQuery(id+"F0.imprint","IMPRINT",EDGE,{"derivedFrom":subQ0}),1.0]])]});}
            extrude(context, id + "F8", {"entities" : qUnion([Q0, Q1, Q2, Q3, Q4, Q5, Q6, Q7, Q8, Q9, Q10, Q11, Q12, Q13, Q14, Q15, Q16, Q17, Q18, Q19, Q20]), "endBound" : BoundingType.SYMMETRIC, "depth" : 5 * mm, "offsetDistance" : 25 * mm});
        }
        {
            var Q0;
            Q0=makeQuery(id+"F1.opExtrude","CAP_FACE",FACE,{"disambiguationData":[OSD([sQuery(id+"F0.wireOp",EDGE,"E4"),sQuery(id+"F0.wireOp",EDGE,"E5.MirrorCS"),sQuery(id+"F0.wireOp",EDGE,"E6.1.0"),sQuery(id+"F0.wireOp",EDGE,"E6.1.1"),sQuery(id+"F0.wireOp",EDGE,"E6.2.0"),sQuery(id+"F0.wireOp",EDGE,"E6.2.1"),sQuery(id+"F0.wireOp",EDGE,"E6.3.0"),sQuery(id+"F0.wireOp",EDGE,"E6.3.1"),sQuery(id+"F0.wireOp",EDGE,"E6.4.0"),sQuery(id+"F0.wireOp",EDGE,"E6.4.1"),sQuery(id+"F0.wireOp",EDGE,"E6.5.0"),sQuery(id+"F0.wireOp",EDGE,"E6.5.1"),sQuery(id+"F0.wireOp",EDGE,"E6.6.0"),sQuery(id+"F0.wireOp",EDGE,"E6.6.1"),sQuery(id+"F0.wireOp",EDGE,"E6.7.0"),sQuery(id+"F0.wireOp",EDGE,"E6.7.1"),sQuery(id+"F0.wireOp",EDGE,"E6.8.0"),sQuery(id+"F0.wireOp",EDGE,"E6.8.1"),sQuery(id+"F0.wireOp",EDGE,"E6.9.0"),sQuery(id+"F0.wireOp",EDGE,"E6.9.1"),sQuery(id+"F0.wireOp",EDGE,"E7.MirrorCS"),sQuery(id+"F0.wireOp",EDGE,"E8.MirrorCS"),sQuery(id+"F0.wireOp",EDGE,"E9.MirrorCS"),sQuery(id+"F0.wireOp",EDGE,"E10.MirrorCS"),sQuery(id+"F0.wireOp",EDGE,"E11.MirrorCS"),sQuery(id+"F0.wireOp",EDGE,"E12.MirrorCS"),sQuery(id+"F0.wireOp",EDGE,"E13.MirrorCS"),sQuery(id+"F0.wireOp",EDGE,"E14.MirrorCS"),sQuery(id+"F0.wireOp",EDGE,"E15.MirrorCS"),sQuery(id+"F0.wireOp",EDGE,"E16.MirrorCS"),sQuery(id+"F0.wireOp",EDGE,"E17.MirrorCS"),sQuery(id+"F0.wireOp",EDGE,"E18.MirrorCS"),sQuery(id+"F0.wireOp",EDGE,"E19.MirrorCS"),sQuery(id+"F0.wireOp",EDGE,"E20.MirrorCS"),sQuery(id+"F0.wireOp",EDGE,"E21.MirrorCS"),sQuery(id+"F0.wireOp",EDGE,"E22.MirrorCS"),sQuery(id+"F0.wireOp",EDGE,"E23.MirrorCS"),sQuery(id+"F0.wireOp",EDGE,"E24.MirrorCS"),sQuery(id+"F0.wireOp",EDGE,"E25.MirrorCS"),sQuery(id+"F0.wireOp",EDGE,"E26.MirrorCS"),sQuery(id+"F0.wireOp",EDGE,"E27")])],"isStart":false});
            var sketch = newSketch(context, id + "F9", { "sketchPlane" : qUnion([Q0])});
            skPoint(sketch, "E87", {"position": v(-2.3, 28.4) * mm});
            skCircle(sketch, "E88", {"center": v(-2.3, 28.4) * mm, "radius": 4.9 * mm});
            skSolve(sketch);
        }
        {
            var Q0;
            Q0=makeQuery(id+"F9.imprint","IMPRINT",FACE,{"disambiguationData":[TD([[makeQuery(id+"F9.imprint","IMPRINT",EDGE,{"derivedFrom":sQuery(id+"F9.wireOp",EDGE,"E88")}),1.0]])]});
            extrude(context, id + "F10", {"entities" : qUnion([Q0]), "depth" : -5 * mm, "offsetDistance" : 25 * mm});
        }
        {
            var Q0;
            Q0=makeQuery(id+"F10.opExtrude","CAP_FACE",FACE,{"disambiguationData":[OSD([sQuery(id+"F9.wireOp",EDGE,"E88")])],"isStart":true});
            extrude(context, id + "F11", {"entities" : qUnion([Q0]), "operationType" : NewBodyOperationType.ADD, "depth" : 4.5 * mm, "offsetDistance" : 25 * mm});
        }
        {
            var Q0;
            Q0=makeQuery(id+"F0.imprint","IMPRINT",FACE,{"disambiguationData":[TD([[makeQuery(id+"F0.imprint","IMPRINT",EDGE,{"derivedFrom":sQuery(id+"F0.wireOp",EDGE,"E27")}),1.0]])]});
            extrude(context, id + "F12", {"entities" : qUnion([Q0]), "operationType" : NewBodyOperationType.ADD, "depth" : 2.5 * mm, "offsetDistance" : 25 * mm});
        }
        {
            var Q0;
            {var subQ0=sQuery(id+"F0.wireOp",EDGE,"E27");Q0=makeQuery(id+"F12.boolean.opBoolean","MERGE",FACE,{"derivedFrom":[makeQuery(id+"F8.opExtrude","CAP_FACE",FACE,{"disambiguationData":[OSD([sQuery(id+"F0.wireOp",EDGE,"E4"),sQuery(id+"F0.wireOp",EDGE,"E5.MirrorCS"),sQuery(id+"F0.wireOp",EDGE,"E6.1.0"),sQuery(id+"F0.wireOp",EDGE,"E6.1.1"),sQuery(id+"F0.wireOp",EDGE,"E6.2.0"),sQuery(id+"F0.wireOp",EDGE,"E6.2.1"),sQuery(id+"F0.wireOp",EDGE,"E6.3.0"),sQuery(id+"F0.wireOp",EDGE,"E6.3.1"),sQuery(id+"F0.wireOp",EDGE,"E6.4.0"),sQuery(id+"F0.wireOp",EDGE,"E6.4.1"),sQuery(id+"F0.wireOp",EDGE,"E6.5.0"),sQuery(id+"F0.wireOp",EDGE,"E6.5.1"),sQuery(id+"F0.wireOp",EDGE,"E6.6.0"),sQuery(id+"F0.wireOp",EDGE,"E6.6.1"),sQuery(id+"F0.wireOp",EDGE,"E6.7.0"),sQuery(id+"F0.wireOp",EDGE,"E6.7.1"),sQuery(id+"F0.wireOp",EDGE,"E6.8.0"),sQuery(id+"F0.wireOp",EDGE,"E6.8.1"),sQuery(id+"F0.wireOp",EDGE,"E6.9.0"),sQuery(id+"F0.wireOp",EDGE,"E6.9.1"),sQuery(id+"F0.wireOp",EDGE,"E7.MirrorCS"),sQuery(id+"F0.wireOp",EDGE,"E8.MirrorCS"),sQuery(id+"F0.wireOp",EDGE,"E9.MirrorCS"),sQuery(id+"F0.wireOp",EDGE,"E10.MirrorCS"),sQuery(id+"F0.wireOp",EDGE,"E11.MirrorCS"),sQuery(id+"F0.wireOp",EDGE,"E12.MirrorCS"),sQuery(id+"F0.wireOp",EDGE,"E13.MirrorCS"),sQuery(id+"F0.wireOp",EDGE,"E14.MirrorCS"),sQuery(id+"F0.wireOp",EDGE,"E15.MirrorCS"),sQuery(id+"F0.wireOp",EDGE,"E16.MirrorCS"),sQuery(id+"F0.wireOp",EDGE,"E17.MirrorCS"),sQuery(id+"F0.wireOp",EDGE,"E18.MirrorCS"),sQuery(id+"F0.wireOp",EDGE,"E19.MirrorCS"),sQuery(id+"F0.wireOp",EDGE,"E20.MirrorCS"),sQuery(id+"F0.wireOp",EDGE,"E21.MirrorCS"),sQuery(id+"F0.wireOp",EDGE,"E22.MirrorCS"),sQuery(id+"F0.wireOp",EDGE,"E23.MirrorCS"),sQuery(id+"F0.wireOp",EDGE,"E24.MirrorCS"),sQuery(id+"F0.wireOp",EDGE,"E25.MirrorCS"),sQuery(id+"F0.wireOp",EDGE,"E26.MirrorCS"),subQ0])],"isStart":false}),makeQuery(id+"F12.opExtrude","CAP_FACE",FACE,{"disambiguationData":[OSD([subQ0])],"isStart":false})]});}
            var sketch = newSketch(context, id + "F13", { "sketchPlane" : qUnion([Q0])});
            skCircle(sketch, "E89", {"center": v(0, 0) * mm, "radius": 4.9 * mm});
            skCircle(sketch, "E90", {"center": v(0, 0) * mm, "radius": 5 * mm});
            skCircle(sketch, "E91", {"center": v(0, 0) * mm, "radius": 9.5 * mm});
            skSolve(sketch);
        }
        {
            var Q0;
            Q0=makeQuery(id+"F13.imprint","IMPRINT",FACE,{"disambiguationData":[TD([[makeQuery(id+"F13.imprint","IMPRINT",EDGE,{"derivedFrom":sQuery(id+"F13.wireOp",EDGE,"E89")}),1.0]])]});
            extrude(context, id + "F14", {"entities" : qUnion([Q0]), "operationType" : NewBodyOperationType.ADD, "depth" : 6.5 * mm, "offsetDistance" : 25 * mm});
        }
        {
            var Q0;
            Q0=makeQuery(id+"F13.imprint","IMPRINT",FACE,{"disambiguationData":[TD([[makeQuery(id+"F13.imprint","IMPRINT",EDGE,{"derivedFrom":sQuery(id+"F13.wireOp",EDGE,"E90")}),-1.0]])]});
            extrude(context, id + "F15", {"entities" : qUnion([Q0]), "depth" : 5 * mm, "offsetDistance" : 25 * mm});
        }
        {
            var Q0;
            Q0=makeQuery(id+"F15.opExtrude","SWEPT_BODY",BODY,{"disambiguationData":[OSD([sQuery(id+"F13.wireOp",EDGE,"E90"),sQuery(id+"F13.wireOp",EDGE,"E91")])]});
            transform(context, id + "F16", {"entities" : qUnion([Q0]), "transformType" : TransformType.TRANSLATION_3D, "dx" : 0 * mm, "dy" : 0 * mm, "dz" : 1.5 * mm, "makeCopy" : false});
        }
        {
            var Q0;
            Q0=makeQuery(id+"F15.opExtrude","CAP_FACE",FACE,{"disambiguationData":[OSD([sQuery(id+"F13.wireOp",EDGE,"E90"),sQuery(id+"F13.wireOp",EDGE,"E91")])],"isStart":false});
            var sketch = newSketch(context, id + "F17", { "sketchPlane" : qUnion([Q0])});
            skCircle(sketch, "E92", {"center": v(0, 0) * mm, "radius": 9.6 * mm});
            skLineSegment(sketch, "E93", {"start": v(-7.18, 28.82) * mm, "end": v(-9.57, 0.81) * mm});
            skLineSegment(sketch, "E94", {"start": v(-9.57, 0.81) * mm, "end": v(9.3, 2.34) * mm, "construction": true});
            skLineSegment(sketch, "E95", {"start": v(9.3, 2.34) * mm, "end": v(2.45, 29.6) * mm});
            skLineSegment(sketch, "E96", {"start": v(2.45, 29.6) * mm, "end": v(-7.18, 28.82) * mm});
            skCircle(sketch, "E97", {"center": v(0, 0) * mm, "radius": 11.5 * mm});
            skLineSegment(sketch, "E98.1.0", {"start": v(4.08, -8.7) * mm, "end": v(-6.68, 6.9) * mm, "construction": true});
            skLineSegment(sketch, "E98.1.1", {"start": v(-21.36, -20.63) * mm, "end": v(4.08, -8.7) * mm});
            skLineSegment(sketch, "E98.1.2", {"start": v(-6.68, 6.9) * mm, "end": v(-26.86, -12.67) * mm});
            skLineSegment(sketch, "E98.1.3", {"start": v(-26.86, -12.67) * mm, "end": v(-21.36, -20.63) * mm});
            skLineSegment(sketch, "E98.2.0", {"start": v(5.49, 7.88) * mm, "end": v(-2.63, -9.23) * mm, "construction": true});
            skLineSegment(sketch, "E98.2.1", {"start": v(28.55, -8.19) * mm, "end": v(5.49, 7.88) * mm});
            skLineSegment(sketch, "E98.2.2", {"start": v(-2.63, -9.23) * mm, "end": v(24.4, -16.92) * mm});
            skLineSegment(sketch, "E98.2.3", {"start": v(24.4, -16.92) * mm, "end": v(28.55, -8.19) * mm});
            skSolve(sketch);
        }
        {
            var Q0;
            {var subQ0=sQuery(id+"F17.wireOp",EDGE,"E96");Q0=makeQuery(id+"F17.imprint","IMPRINT",FACE,{"disambiguationData":[TD([[makeQuery(id+"F17.imprint","IMPRINT",EDGE,{"derivedFrom":subQ0}),1.0]])]});}
            var Q1;
            {var subQ7=sQuery(id+"F17.wireOp",EDGE,"E98.1.2");var subQ9=sQuery(id+"F17.wireOp",EDGE,"E92");var subQ10=makeQuery(id+"F17.imprint","INTERSECT",VERTEX,{"derivedFrom":[subQ9,subQ7]});Q1=makeQuery(id+"F17.imprint","IMPRINT",FACE,{"disambiguationData":[TD([[makeQuery(id+"F17.imprint","IMPRINT",EDGE,{"disambiguationData":[TD([[subQ10,1.0]])],"derivedFrom":subQ9}),-1.0]])]});}
            var Q2;
            {var subQ0=sQuery(id+"F17.wireOp",EDGE,"E97");var subQ1=sQuery(id+"F17.wireOp",EDGE,"E93");var subQ2=makeQuery(id+"F17.imprint","INTERSECT",VERTEX,{"derivedFrom":[subQ1,subQ0]});Q2=makeQuery(id+"F17.imprint","IMPRINT",FACE,{"disambiguationData":[TD([[makeQuery(id+"F17.imprint","IMPRINT",EDGE,{"disambiguationData":[TD([[subQ2,-1.0]])],"derivedFrom":subQ1}),-1.0]])]});}
            var Q3;
            {var subQ7=sQuery(id+"F17.wireOp",EDGE,"E93");var subQ8=sQuery(id+"F17.wireOp",EDGE,"E92");var subQ9=makeQuery(id+"F17.imprint","INTERSECT",VERTEX,{"derivedFrom":[subQ8,subQ7]});Q3=makeQuery(id+"F17.imprint","IMPRINT",FACE,{"disambiguationData":[TD([[makeQuery(id+"F17.imprint","IMPRINT",EDGE,{"disambiguationData":[TD([[subQ9,-1.0]])],"derivedFrom":subQ8}),-1.0]])]});}
            var Q4;
            {var subQ5=sQuery(id+"F17.wireOp",EDGE,"E98.1.3");Q4=makeQuery(id+"F17.imprint","IMPRINT",FACE,{"disambiguationData":[TD([[makeQuery(id+"F17.imprint","IMPRINT",EDGE,{"derivedFrom":subQ5}),1.0]])]});}
            var Q5;
            {var subQ0=sQuery(id+"F17.wireOp",EDGE,"E93");var subQ1=sQuery(id+"F17.wireOp",EDGE,"E92");var subQ2=makeQuery(id+"F17.imprint","INTERSECT",VERTEX,{"derivedFrom":[subQ1,subQ0]});Q5=makeQuery(id+"F17.imprint","IMPRINT",FACE,{"disambiguationData":[TD([[makeQuery(id+"F17.imprint","IMPRINT",EDGE,{"disambiguationData":[TD([[subQ2,1.0]])],"derivedFrom":subQ1}),-1.0]])]});}
            var Q6;
            {var subQ0=sQuery(id+"F17.wireOp",EDGE,"E98.1.1");var subQ1=sQuery(id+"F17.wireOp",EDGE,"E92");var subQ2=makeQuery(id+"F17.imprint","INTERSECT",VERTEX,{"derivedFrom":[subQ1,subQ0]});Q6=makeQuery(id+"F17.imprint","IMPRINT",FACE,{"disambiguationData":[TD([[makeQuery(id+"F17.imprint","IMPRINT",EDGE,{"disambiguationData":[TD([[subQ2,1.0]])],"derivedFrom":subQ1}),-1.0]])]});}
            var Q7;
            {var subQ0=sQuery(id+"F17.wireOp",EDGE,"E95");var subQ1=sQuery(id+"F17.wireOp",EDGE,"E92");var subQ2=makeQuery(id+"F17.imprint","INTERSECT",VERTEX,{"derivedFrom":[subQ1,subQ0]});Q7=makeQuery(id+"F17.imprint","IMPRINT",FACE,{"disambiguationData":[TD([[makeQuery(id+"F17.imprint","IMPRINT",EDGE,{"disambiguationData":[TD([[subQ2,-1.0]])],"derivedFrom":subQ1}),-1.0]])]});}
            var Q8;
            {var subQ0=sQuery(id+"F17.wireOp",EDGE,"E97");var subQ1=sQuery(id+"F17.wireOp",EDGE,"E95");var subQ2=makeQuery(id+"F17.imprint","INTERSECT",VERTEX,{"derivedFrom":[subQ1,subQ0]});Q8=makeQuery(id+"F17.imprint","IMPRINT",FACE,{"disambiguationData":[TD([[makeQuery(id+"F17.imprint","IMPRINT",EDGE,{"disambiguationData":[TD([[subQ2,1.0]])],"derivedFrom":subQ1}),-1.0]])]});}
            var Q9;
            {var subQ1=sQuery(id+"F17.wireOp",EDGE,"E92");var subQ9=sQuery(id+"F17.wireOp",EDGE,"E95");var subQ10=makeQuery(id+"F17.imprint","INTERSECT",VERTEX,{"derivedFrom":[subQ1,subQ9]});Q9=makeQuery(id+"F17.imprint","IMPRINT",FACE,{"disambiguationData":[TD([[makeQuery(id+"F17.imprint","IMPRINT",EDGE,{"disambiguationData":[TD([[subQ10,1.0]])],"derivedFrom":subQ1}),-1.0]])]});}
            var Q10;
            {var subQ0=sQuery(id+"F17.wireOp",EDGE,"E98.1.1");var subQ1=sQuery(id+"F17.wireOp",EDGE,"E97");var subQ2=makeQuery(id+"F17.imprint","INTERSECT",VERTEX,{"derivedFrom":[subQ1,subQ0]});Q10=makeQuery(id+"F17.imprint","IMPRINT",FACE,{"disambiguationData":[TD([[makeQuery(id+"F17.imprint","IMPRINT",EDGE,{"disambiguationData":[TD([[subQ2,-1.0]])],"derivedFrom":subQ1}),1.0]])]});}
            var Q11;
            {var subQ5=sQuery(id+"F17.wireOp",EDGE,"E98.2.3");Q11=makeQuery(id+"F17.imprint","IMPRINT",FACE,{"disambiguationData":[TD([[makeQuery(id+"F17.imprint","IMPRINT",EDGE,{"derivedFrom":subQ5}),1.0]])]});}
            extrude(context, id + "F18", {"entities" : qUnion([Q0, Q1, Q2, Q3, Q4, Q5, Q6, Q7, Q8, Q9, Q10, Q11]), "operationType" : NewBodyOperationType.ADD, "oppositeDirection" : true, "depth" : 3.5 * mm, "offsetDistance" : 25 * mm});
        }
    });
